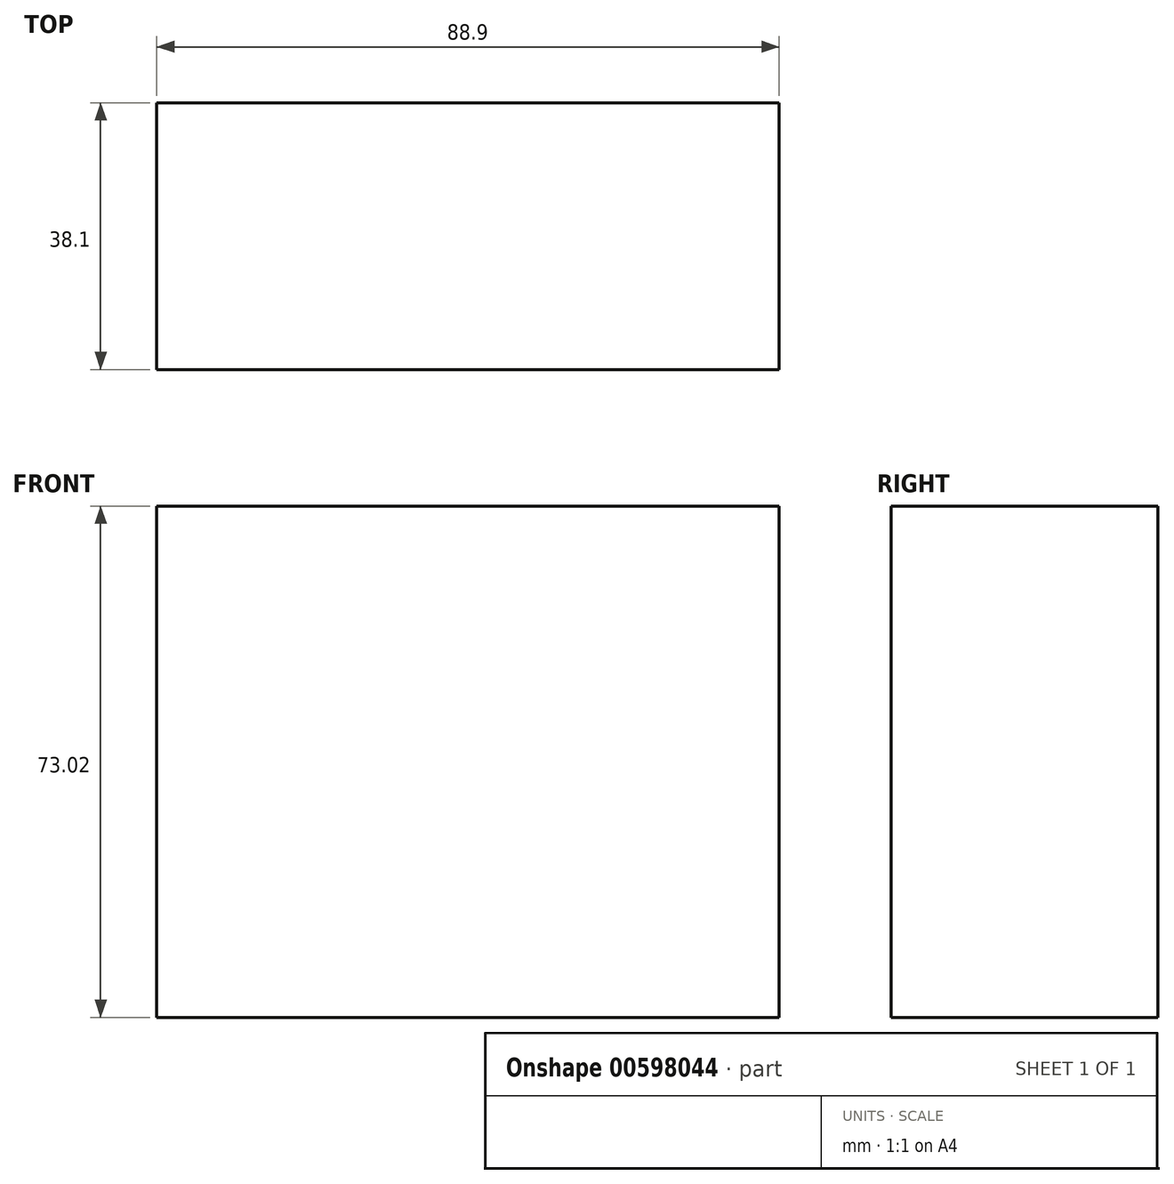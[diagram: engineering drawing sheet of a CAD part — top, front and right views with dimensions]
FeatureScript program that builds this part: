
annotation { "Feature Type Name" : "Feature", "Feature Type Description" : "" }
export const myFeature = defineFeature(function(context is Context, id is Id, definition is map)
    precondition{}
    {
        {
            var Q0;
            Q0=qCreatedBy(makeId("Front.planeOp"),FACE);
            var sketch = newSketch(context, id + "F0", { "sketchPlane" : qUnion([Q0])});
            skLineSegment(sketch, "E0.bottom", {"start": v(44.45, 36.51) * mm, "end": v(-44.45, 36.51) * mm});
            skLineSegment(sketch, "E0.top", {"start": v(44.45, -36.51) * mm, "end": v(-44.45, -36.51) * mm});
            skLineSegment(sketch, "E0.left", {"start": v(44.45, 36.51) * mm, "end": v(44.45, -36.51) * mm});
            skLineSegment(sketch, "E0.right", {"start": v(-44.45, 36.51) * mm, "end": v(-44.45, -36.51) * mm});
            skPoint(sketch, "E0.middle", {"position": v(0, 0) * mm});
            skSolve(sketch);
        }
        {
            var Q0;
            Q0 = qSketchRegion(id + "F0", true);
            extrude(context, id + "F1", {"entities" : qUnion([Q0]), "endBound" : BoundingType.SYMMETRIC, "depth" : 38.1 * mm, "offsetDistance" : 25.4 * mm});
        }
    });
